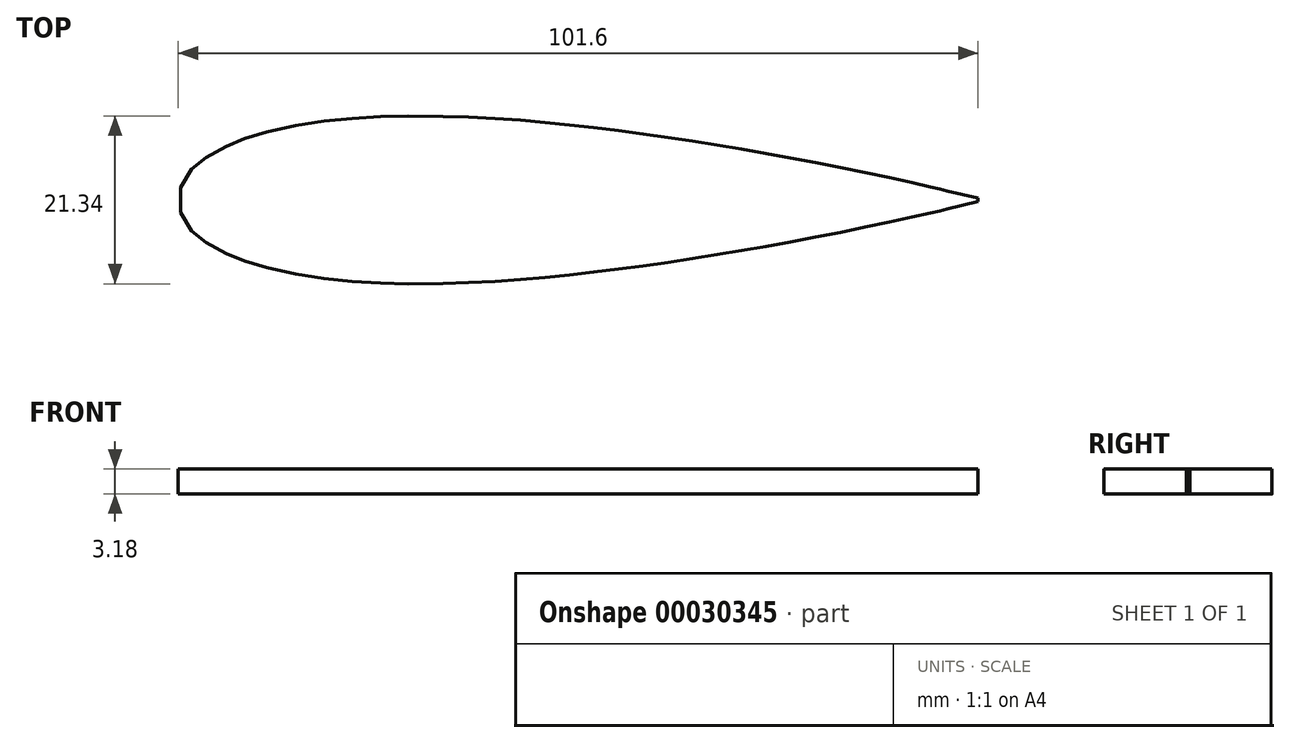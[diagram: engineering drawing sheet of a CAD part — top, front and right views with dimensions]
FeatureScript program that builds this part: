
annotation { "Feature Type Name" : "Feature", "Feature Type Description" : "" }
export const myFeature = defineFeature(function(context is Context, id is Id, definition is map)
    precondition{}
    {
        {
            var Q0;
            Q0=qCreatedBy(makeId("Top.planeOp"),FACE);
            var sketch = newSketch(context, id + "F0", { "sketchPlane" : qUnion([Q0])});
            skFitSpline(sketch, "E0", {"points": [v(101.6, 0.22) * mm, v(96.52, 1.43) * mm, v(91.44, 2.57) * mm, v(81.28, 4.66) * mm, v(71.12, 6.51) * mm, v(60.96, 8.11) * mm, v(50.8, 9.41) * mm, v(40.64, 10.32) * mm, v(30.48, 10.67) * mm, v(25.4, 10.56) * mm, v(20.32, 10.2) * mm, v(15.24, 9.5) * mm, v(10.16, 8.33) * mm, v(7.62, 7.47) * mm, v(5.08, 6.32) * mm, v(2.54, 4.65) * mm, v(1.27, 3.37) * mm, v(0, 0) * mm, v(1.27, -3.37) * mm, v(2.54, -4.65) * mm, v(5.08, -6.32) * mm, v(7.62, -7.47) * mm, v(10.16, -8.33) * mm, v(15.24, -9.5) * mm, v(20.32, -10.2) * mm, v(25.4, -10.56) * mm, v(30.48, -10.67) * mm, v(40.64, -10.32) * mm, v(50.8, -9.41) * mm, v(60.96, -8.11) * mm, v(71.12, -6.51) * mm, v(81.28, -4.66) * mm, v(91.44, -2.57) * mm, v(96.52, -1.43) * mm, v(101.6, -0.22) * mm], "startDerivative": vector(-548.74, 130.7) * mm, "endDerivative": vector(548.74, 130.7) * mm});
            skLineSegment(sketch, "E1", {"start": v(101.6, 0.22) * mm, "end": v(101.6, -0.22) * mm});
            skArc(sketch, "E2", {"start": v(1.1, 3.13) * mm, "mid": v(-0.01, 0) * mm, "end": v(1.1, -3.13) * mm, "construction": true});
            skLineSegment(sketch, "E3", {"start": v(33.65, 10.62) * mm, "end": v(33.65, 4.45) * mm});
            skLineSegment(sketch, "E4", {"start": v(33.65, 4.45) * mm, "end": v(30.48, 4.45) * mm});
            skLineSegment(sketch, "E5", {"start": v(30.48, 4.45) * mm, "end": v(30.48, -4.45) * mm});
            skLineSegment(sketch, "E6", {"start": v(30.48, -4.45) * mm, "end": v(33.65, -4.45) * mm});
            skLineSegment(sketch, "E7", {"start": v(33.65, -4.45) * mm, "end": v(33.65, -10.62) * mm});
            skSolve(sketch);
        }
        {
            var Q0;
            Q0 = qSketchRegion(id + "F0", true);
            extrude(context, id + "F1", {"entities" : qUnion([Q0]), "depth" : 3.17 * mm});
        }
    });
